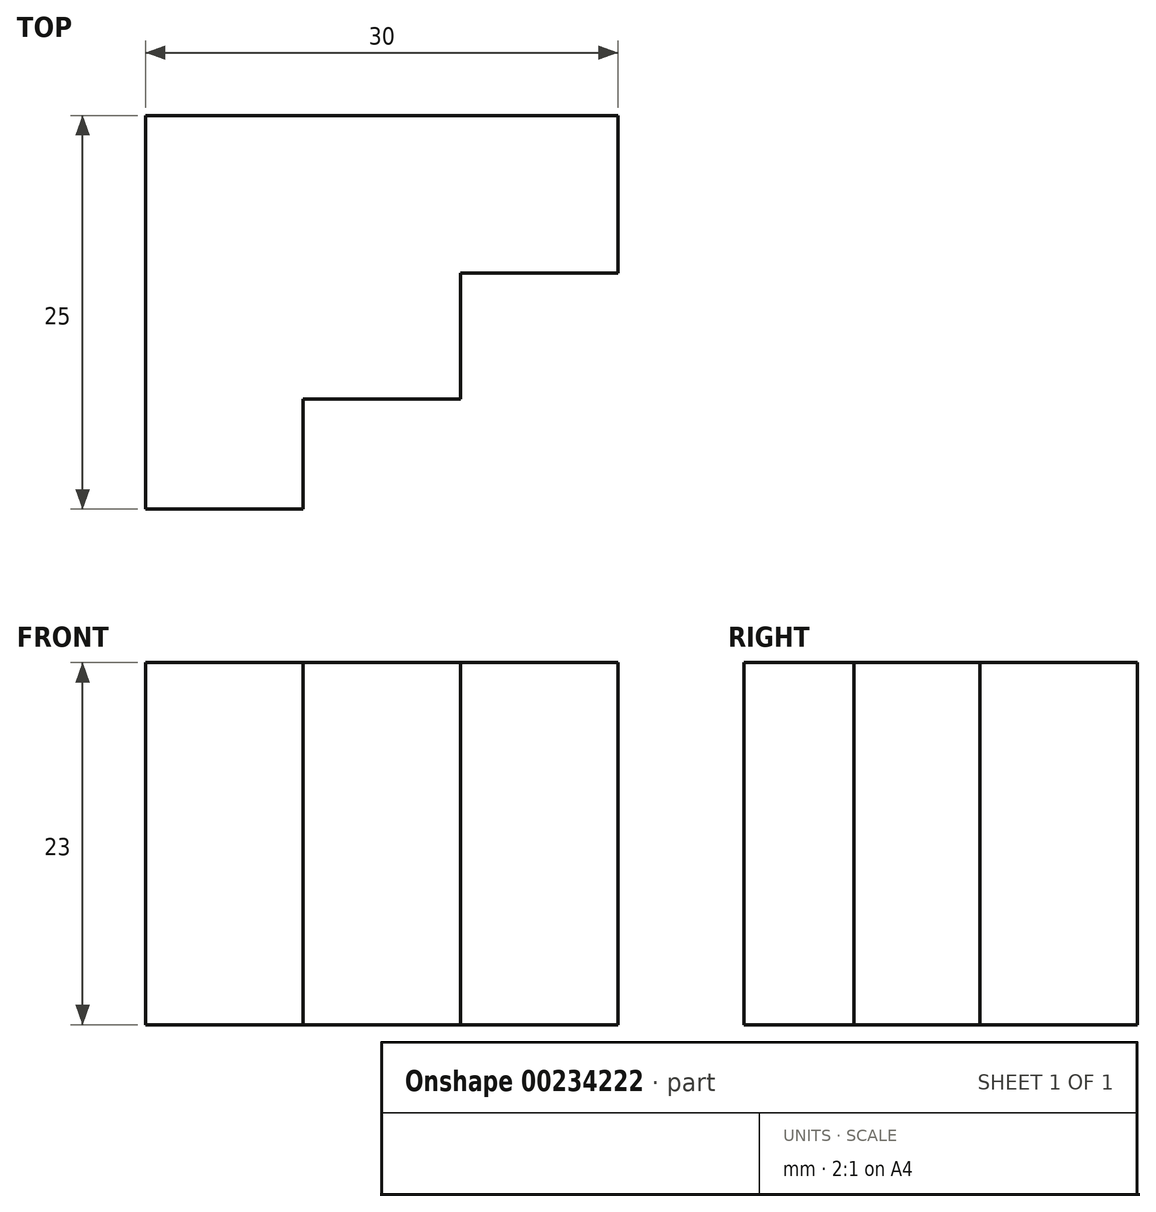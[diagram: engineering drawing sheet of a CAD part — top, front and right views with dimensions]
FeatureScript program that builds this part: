
annotation { "Feature Type Name" : "Feature", "Feature Type Description" : "" }
export const myFeature = defineFeature(function(context is Context, id is Id, definition is map)
    precondition{}
    {
        {
            var Q0;
            Q0=qCreatedBy(makeId("Top.planeOp"),FACE);
            var sketch = newSketch(context, id + "F0", { "sketchPlane" : qUnion([Q0])});
            skLineSegment(sketch, "E0", {"start": v(0, 0) * mm, "end": v(0, 25) * mm});
            skLineSegment(sketch, "E1", {"start": v(0, 25) * mm, "end": v(30, 25) * mm});
            skLineSegment(sketch, "E2", {"start": v(30, 25) * mm, "end": v(30, 15) * mm});
            skLineSegment(sketch, "E3", {"start": v(30, 15) * mm, "end": v(20, 15) * mm});
            skLineSegment(sketch, "E4", {"start": v(20, 15) * mm, "end": v(20, 7) * mm});
            skLineSegment(sketch, "E5", {"start": v(20, 7) * mm, "end": v(10, 7) * mm});
            skLineSegment(sketch, "E6", {"start": v(10, 7) * mm, "end": v(10, 0) * mm});
            skLineSegment(sketch, "E7", {"start": v(0, 0) * mm, "end": v(10, 0) * mm});
            skSolve(sketch);
        }
        {
            var Q0;
            Q0=makeQuery(id+"F0.imprint","IMPRINT",FACE,{"disambiguationData":[TD([[makeQuery(id+"F0.imprint","IMPRINT",EDGE,{"derivedFrom":sQuery(id+"F0.wireOp",EDGE,"E0")}),-1.0]])]});
            extrude(context, id + "F1", {"entities" : qUnion([Q0]), "depth" : 23 * mm});
        }
    });
